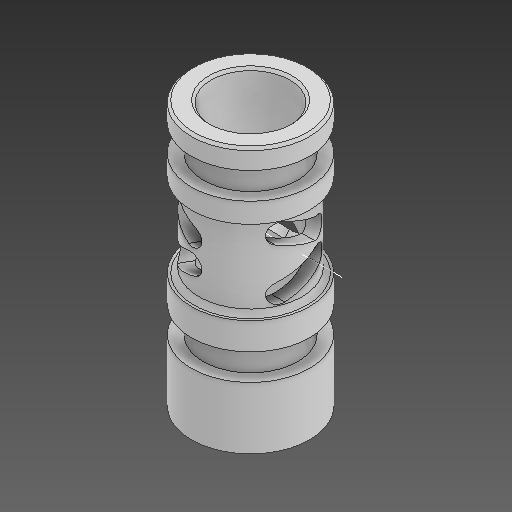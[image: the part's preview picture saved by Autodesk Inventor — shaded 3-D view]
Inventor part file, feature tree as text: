
AUTODESK INVENTOR PART (.ipt)
format: ipt  version: 2021 (Build 250183000, 183)  size: 298,496 bytes
history: native  units: in
note: dims shown in document units (in); Inventor stores cm internally (conversion verified against a paired STEP export)
features: other x7, sketch x5, plane x1
ambient origin geometry x8: Origin, YZ Plane, XZ Plane, XY Plane, X Axis, Y Axis, Z Axis, Center Point
bodies: Solid1 (feature_tree)
feature tree (13):
  other  "outer_sleeve.ipt"
  other  "Solid1::outer_sleeve.ipt"
  other  "TaggingFeature1"
  sketch  "Sketch2"  dims[d0=0.3937in]
  sketch  "Sketch3"
  sketch  "Sketch4"
  sketch  "Sketch5"
  sketch  "Sketch10"
  plane  "Work Plane1"
  other  "Work Axis1"
  other  "Work Axis2"
  other  "Srf1"
  other  "Srf1::Derived"
